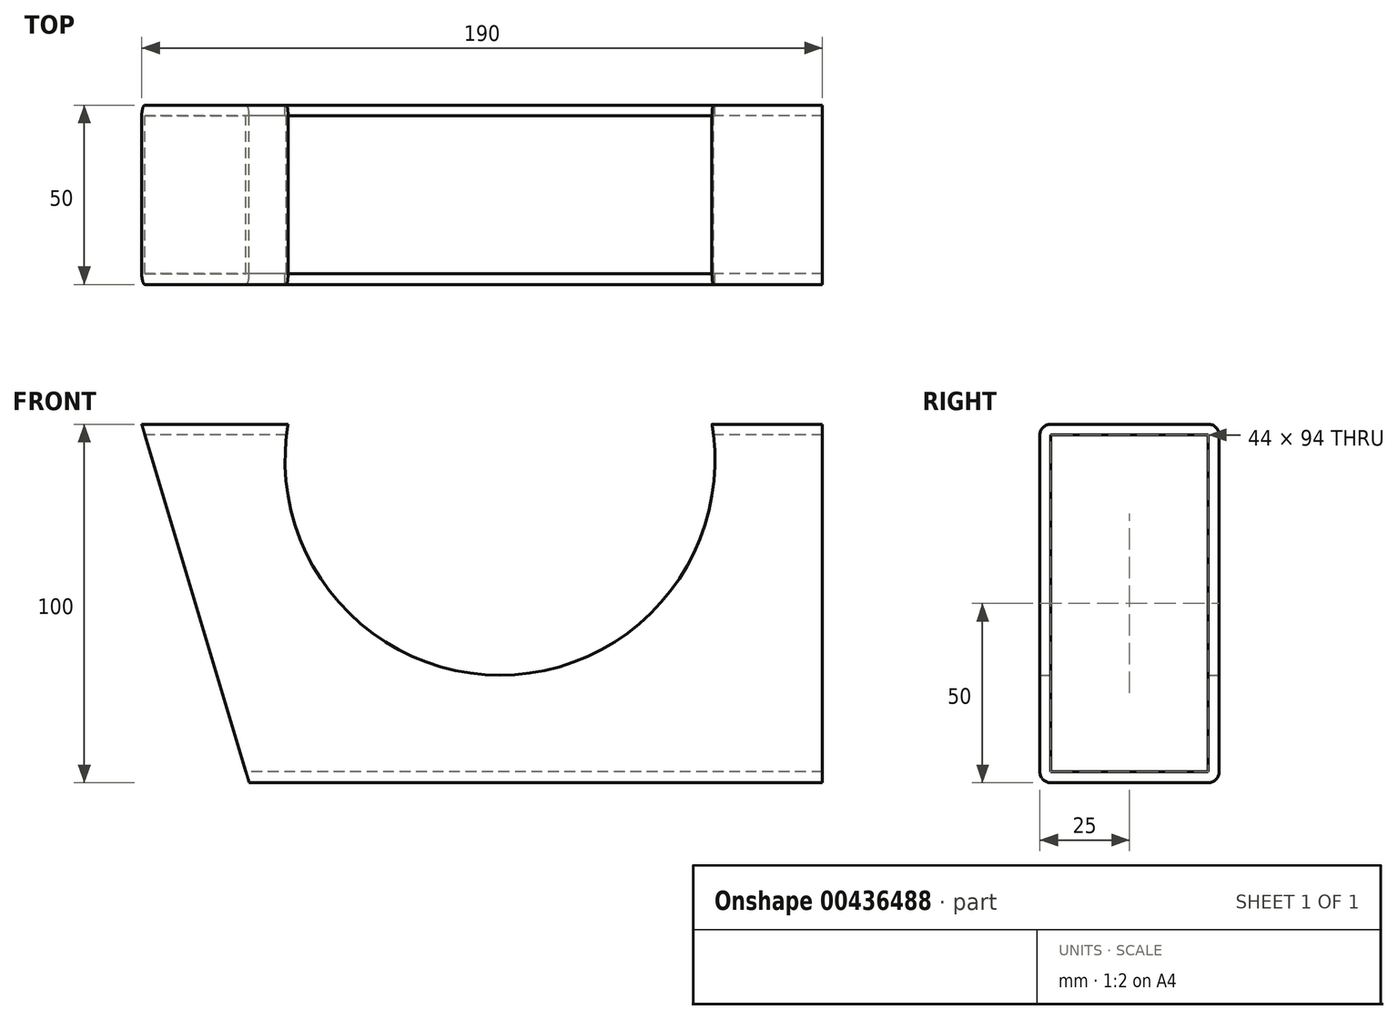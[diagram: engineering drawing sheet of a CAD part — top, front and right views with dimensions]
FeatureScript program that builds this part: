
annotation { "Feature Type Name" : "Feature", "Feature Type Description" : "" }
export const myFeature = defineFeature(function(context is Context, id is Id, definition is map)
    precondition{}
    {
        {
            var Q0;
            Q0=qCreatedBy(makeId("Right.planeOp"),FACE);
            var sketch = newSketch(context, id + "F0", { "sketchPlane" : qUnion([Q0])});
            skLineSegment(sketch, "E0.bottom", {"start": v(-22, 50) * mm, "end": v(22, 50) * mm});
            skLineSegment(sketch, "E0.top", {"start": v(-22, -50) * mm, "end": v(22, -50) * mm});
            skLineSegment(sketch, "E0.left", {"start": v(-25, 47) * mm, "end": v(-25, -47) * mm});
            skLineSegment(sketch, "E0.right", {"start": v(25, 47) * mm, "end": v(25, -47) * mm});
            skLineSegment(sketch, "E1", {"start": v(25, 50) * mm, "end": v(-25, -50) * mm, "construction": true});
            skLineSegment(sketch, "E2", {"start": v(-25, 50) * mm, "end": v(25, -50) * mm, "construction": true});
            skLineSegment(sketch, "E3.0", {"start": v(-22, 47) * mm, "end": v(22, 47) * mm});
            skLineSegment(sketch, "E3.1", {"start": v(-22, 47) * mm, "end": v(-22, -47) * mm});
            skLineSegment(sketch, "E3.2", {"start": v(-22, -47) * mm, "end": v(22, -47) * mm});
            skLineSegment(sketch, "E3.3", {"start": v(22, 47) * mm, "end": v(22, -47) * mm});
            skPoint(sketch, "E4.visualSharp", {"position": v(-25, 50) * mm});
            skArc(sketch, "E4.filletArc", {"start": v(-22, 50) * mm, "mid": v(-24.12, 49.12) * mm, "end": v(-25, 47) * mm});
            skPoint(sketch, "E5.visualSharp", {"position": v(25, 50) * mm});
            skArc(sketch, "E5.filletArc", {"start": v(25, 47) * mm, "mid": v(24.12, 49.12) * mm, "end": v(22, 50) * mm});
            skPoint(sketch, "E6.visualSharp", {"position": v(25, -50) * mm});
            skArc(sketch, "E6.filletArc", {"start": v(22, -50) * mm, "mid": v(24.12, -49.12) * mm, "end": v(25, -47) * mm});
            skPoint(sketch, "E7.visualSharp", {"position": v(-25, -50) * mm});
            skArc(sketch, "E7.filletArc", {"start": v(-25, -47) * mm, "mid": v(-24.12, -49.12) * mm, "end": v(-22, -50) * mm});
            skSolve(sketch);
        }
        {
            var Q0;
            Q0=makeQuery(id+"F0.imprint","IMPRINT",FACE,{"disambiguationData":[TD([[makeQuery(id+"F0.imprint","IMPRINT",EDGE,{"derivedFrom":sQuery(id+"F0.wireOp",EDGE,"E0.bottom")}),-1.0]])]});
            extrude(context, id + "F1", {"entities" : qUnion([Q0]), "depth" : 190 * mm});
        }
        {
            var Q0;
            Q0=qCreatedBy(makeId("Front.planeOp"),FACE);
            var sketch = newSketch(context, id + "F2", { "sketchPlane" : qUnion([Q0])});
            skLineSegment(sketch, "E8", {"start": v(0, 50) * mm, "end": v(30, -50) * mm});
            skLineSegment(sketch, "E9", {"start": v(30, -50) * mm, "end": v(0, -50) * mm});
            skLineSegment(sketch, "E10", {"start": v(0, -50) * mm, "end": v(0, 50) * mm});
            skSolve(sketch);
        }
        {
            var Q0;
            Q0 = qSketchRegion(id + "F2", true);
            extrude(context, id + "F3", {"entities" : qUnion([Q0]), "operationType" : NewBodyOperationType.REMOVE, "endBound" : BoundingType.THROUGH_ALL, "depth" : 25.4 * mm, "hasSecondDirection" : true, "secondDirectionBound" : BoundingType.THROUGH_ALL, "secondDirectionOppositeDirection" : true, "secondDirectionDepth" : 25.4 * mm});
        }
        {
            var Q0;
            Q0=qCreatedBy(makeId("Front.planeOp"),FACE);
            var sketch = newSketch(context, id + "F4", { "sketchPlane" : qUnion([Q0])});
            skArc(sketch, "E11", {"start": v(40.84, 50) * mm, "mid": v(100, -20) * mm, "end": v(159.16, 50) * mm});
            skLineSegment(sketch, "E12", {"start": v(40.84, 50) * mm, "end": v(159.16, 50) * mm});
            skSolve(sketch);
        }
        {
            var Q0;
            Q0 = qSketchRegion(id + "F4", true);
            extrude(context, id + "F5", {"entities" : qUnion([Q0]), "operationType" : NewBodyOperationType.REMOVE, "endBound" : BoundingType.THROUGH_ALL, "depth" : 25.4 * mm, "hasSecondDirection" : true, "secondDirectionBound" : BoundingType.THROUGH_ALL, "secondDirectionOppositeDirection" : true, "secondDirectionDepth" : 25.4 * mm});
        }
    });
